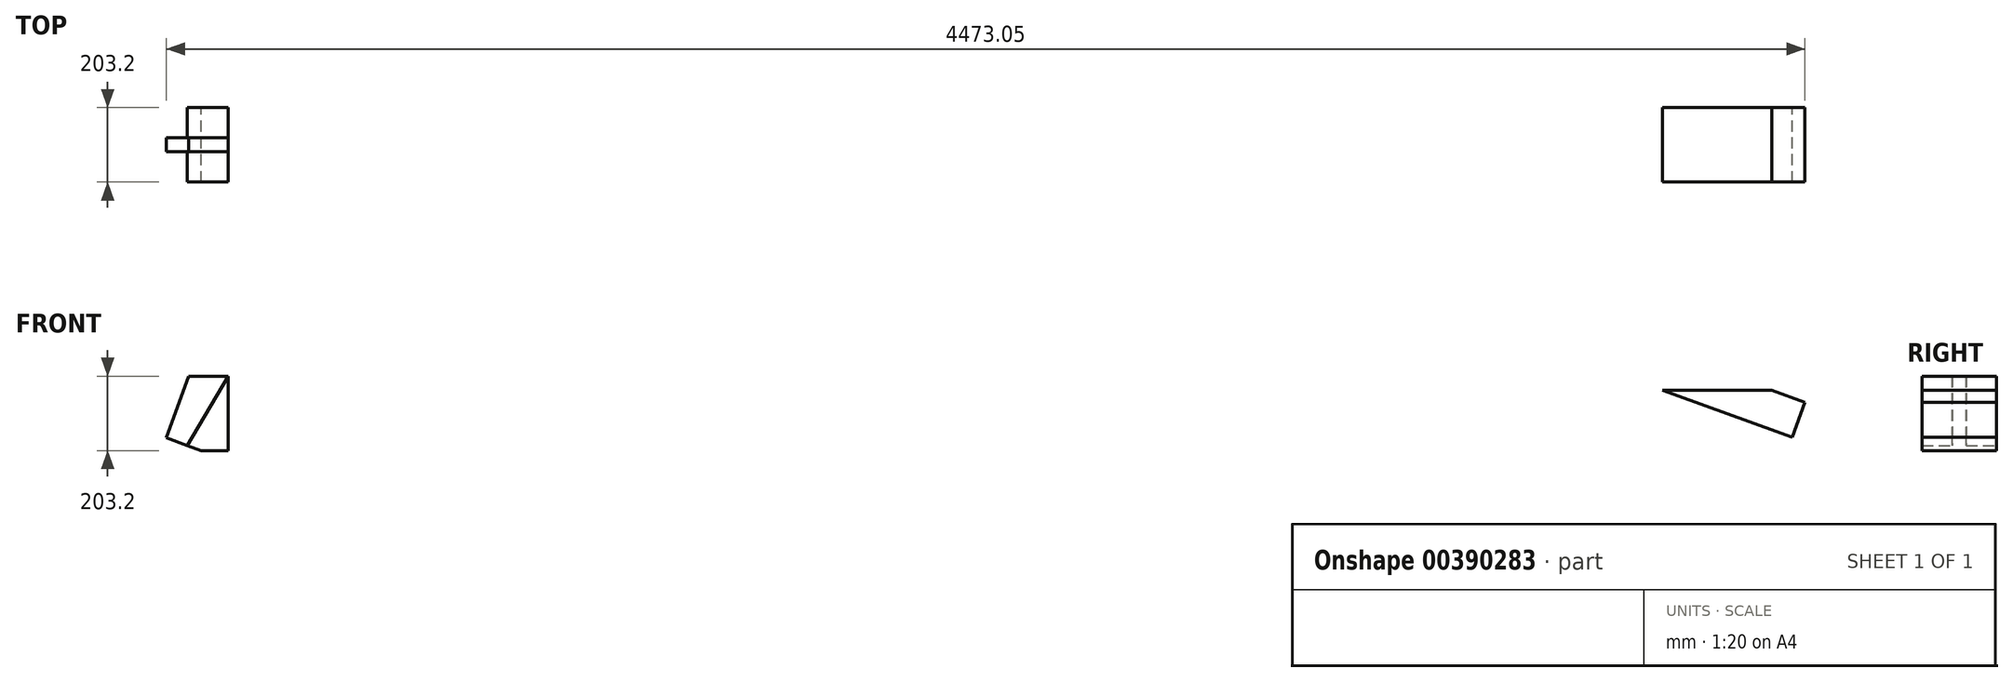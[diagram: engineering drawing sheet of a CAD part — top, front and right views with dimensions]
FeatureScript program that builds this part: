
annotation { "Feature Type Name" : "Feature", "Feature Type Description" : "" }
export const myFeature = defineFeature(function(context is Context, id is Id, definition is map)
    precondition{}
    {
        {
            var Q0;
            Q0=qCreatedBy(makeId("Front.planeOp"),FACE);
            var sketch = newSketch(context, id + "F0", { "sketchPlane" : qUnion([Q0])});
            skLineSegment(sketch, "E0.bottom", {"start": v(-2403.9, 101.6) * mm, "end": v(2403.9, 101.6) * mm});
            skLineSegment(sketch, "E0.top", {"start": v(-2403.9, -101.6) * mm, "end": v(2403.9, -101.6) * mm});
            skLineSegment(sketch, "E0.left", {"start": v(-2403.9, 101.6) * mm, "end": v(-2403.9, -101.6) * mm});
            skLineSegment(sketch, "E0.right", {"start": v(2403.9, 101.6) * mm, "end": v(2403.9, -101.6) * mm});
            skPoint(sketch, "E0.middle", {"position": v(0, 0) * mm});
            skLineSegment(sketch, "E1", {"start": v(2403.9, -101.6) * mm, "end": v(1843.7, 101.6) * mm});
            skLineSegment(sketch, "E2", {"start": v(2302.89, -64.96) * mm, "end": v(1909.53, 77.72) * mm});
            skLineSegment(sketch, "E3", {"start": v(2289.6, -101.6) * mm, "end": v(2337.53, 30.55) * mm});
            skLineSegment(sketch, "E4", {"start": v(2337.53, 30.55) * mm, "end": v(2141.66, 101.6) * mm});
            skLineSegment(sketch, "E5", {"start": v(2141.66, 101.6) * mm, "end": v(1918.2, 101.6) * mm});
            skLineSegment(sketch, "E6", {"start": v(-1966.3, 101.6) * mm, "end": v(-1966.3, -101.6) * mm});
            skLineSegment(sketch, "E7", {"start": v(-1966.3, 101.6) * mm, "end": v(-2040, -101.6) * mm});
            skLineSegment(sketch, "E8", {"start": v(-1966.3, 101.6) * mm, "end": v(-2079.75, -89.55) * mm});
            skLineSegment(sketch, "E9", {"start": v(-2079.75, -89.55) * mm, "end": v(-2040, -101.6) * mm});
            skLineSegment(sketch, "E10", {"start": v(-2040, -101.6) * mm, "end": v(-2135.52, -66.95) * mm});
            skLineSegment(sketch, "E11", {"start": v(-2135.52, -66.95) * mm, "end": v(-2074.38, 101.6) * mm});
            skLineSegment(sketch, "E12", {"start": v(1948.74, 63.5) * mm, "end": v(2246.7, 63.5) * mm});
            skLineSegment(sketch, "E13", {"start": v(2315.88, -29.14) * mm, "end": v(1843.7, 101.6) * mm});
            skSolve(sketch);
        }
        {
            var Q0;
            {var subQ0=sQuery(id+"F0.wireOp",EDGE,"E2");Q0=makeQuery(id+"F0.imprint","IMPRINT",FACE,{"disambiguationData":[TD([[makeQuery(id+"F0.imprint","IMPRINT",EDGE,{"derivedFrom":subQ0}),1.0]])]});}
            var Q1;
            {var subQ0=sQuery(id+"F0.wireOp",EDGE,"E6");Q1=makeQuery(id+"F0.imprint","IMPRINT",FACE,{"disambiguationData":[TD([[makeQuery(id+"F0.imprint","IMPRINT",EDGE,{"derivedFrom":subQ0}),-1.0]])]});}
            var Q2;
            {var subQ0=sQuery(id+"F0.wireOp",EDGE,"E7");Q2=makeQuery(id+"F0.imprint","IMPRINT",FACE,{"disambiguationData":[TD([[makeQuery(id+"F0.imprint","IMPRINT",EDGE,{"derivedFrom":subQ0}),-1.0]])]});}
            var Q3;
            {var subQ1=sQuery(id+"F0.wireOp",EDGE,"E2");var subQ3=sQuery(id+"F0.wireOp",EDGE,"E12");var subQ4=makeQuery(id+"F0.imprint","INTERSECT",VERTEX,{"derivedFrom":[subQ1,subQ3]});Q3=makeQuery(id+"F0.imprint","IMPRINT",FACE,{"disambiguationData":[TD([[makeQuery(id+"F0.imprint","IMPRINT",EDGE,{"disambiguationData":[TD([[subQ4,-1.0]])],"derivedFrom":subQ3}),-1.0]])]});}
            var Q4;
            {var subQ1=sQuery(id+"F0.wireOp",EDGE,"E1");var subQ3=sQuery(id+"F0.wireOp",EDGE,"E2");var subQ4=makeQuery(id+"F0.imprint","INTERSECT",VERTEX,{"derivedFrom":[subQ1,subQ3]});Q4=makeQuery(id+"F0.imprint","IMPRINT",FACE,{"disambiguationData":[TD([[makeQuery(id+"F0.imprint","IMPRINT",EDGE,{"disambiguationData":[TD([[subQ4,1.0]])],"derivedFrom":subQ3}),-1.0]])]});}
            extrude(context, id + "F1", {"entities" : qUnion([Q0, Q1, Q2, Q3, Q4]), "endBound" : BoundingType.SYMMETRIC, "depth" : 203.2 * mm});
        }
        {
            var Q0;
            {var subQ0=sQuery(id+"F0.wireOp",EDGE,"E8");Q0=makeQuery(id+"F0.imprint","IMPRINT",FACE,{"disambiguationData":[TD([[makeQuery(id+"F0.imprint","IMPRINT",EDGE,{"derivedFrom":subQ0}),-1.0]])]});}
            var Q1;
            {var subQ2=sQuery(id+"F0.wireOp",EDGE,"E2");Q1=makeQuery(id+"F0.imprint","IMPRINT",FACE,{"disambiguationData":[TD([[makeQuery(id+"F0.imprint","IMPRINT",EDGE,{"derivedFrom":subQ2}),-1.0]])]});}
            var Q2;
            {var subQ5=sQuery(id+"F0.wireOp",EDGE,"E5");Q2=makeQuery(id+"F0.imprint","IMPRINT",FACE,{"disambiguationData":[TD([[makeQuery(id+"F0.imprint","IMPRINT",EDGE,{"derivedFrom":subQ5}),1.0]])]});}
            var Q3;
            {var subQ0=sQuery(id+"F0.wireOp",EDGE,"E4");var subQ1=sQuery(id+"F0.wireOp",EDGE,"E3");var subQ2=makeQuery(id+"F0.imprint","INTERSECT",VERTEX,{"derivedFrom":[subQ1,subQ0]});Q3=makeQuery(id+"F0.imprint","IMPRINT",FACE,{"disambiguationData":[TD([[makeQuery(id+"F0.imprint","IMPRINT",EDGE,{"disambiguationData":[TD([[subQ2,1.0]])],"derivedFrom":subQ1}),1.0]])]});}
            extrude(context, id + "F2", {"entities" : qUnion([Q0, Q1, Q2, Q3]), "operationType" : NewBodyOperationType.ADD, "endBound" : BoundingType.SYMMETRIC, "depth" : 38.1 * mm});
        }
    });
